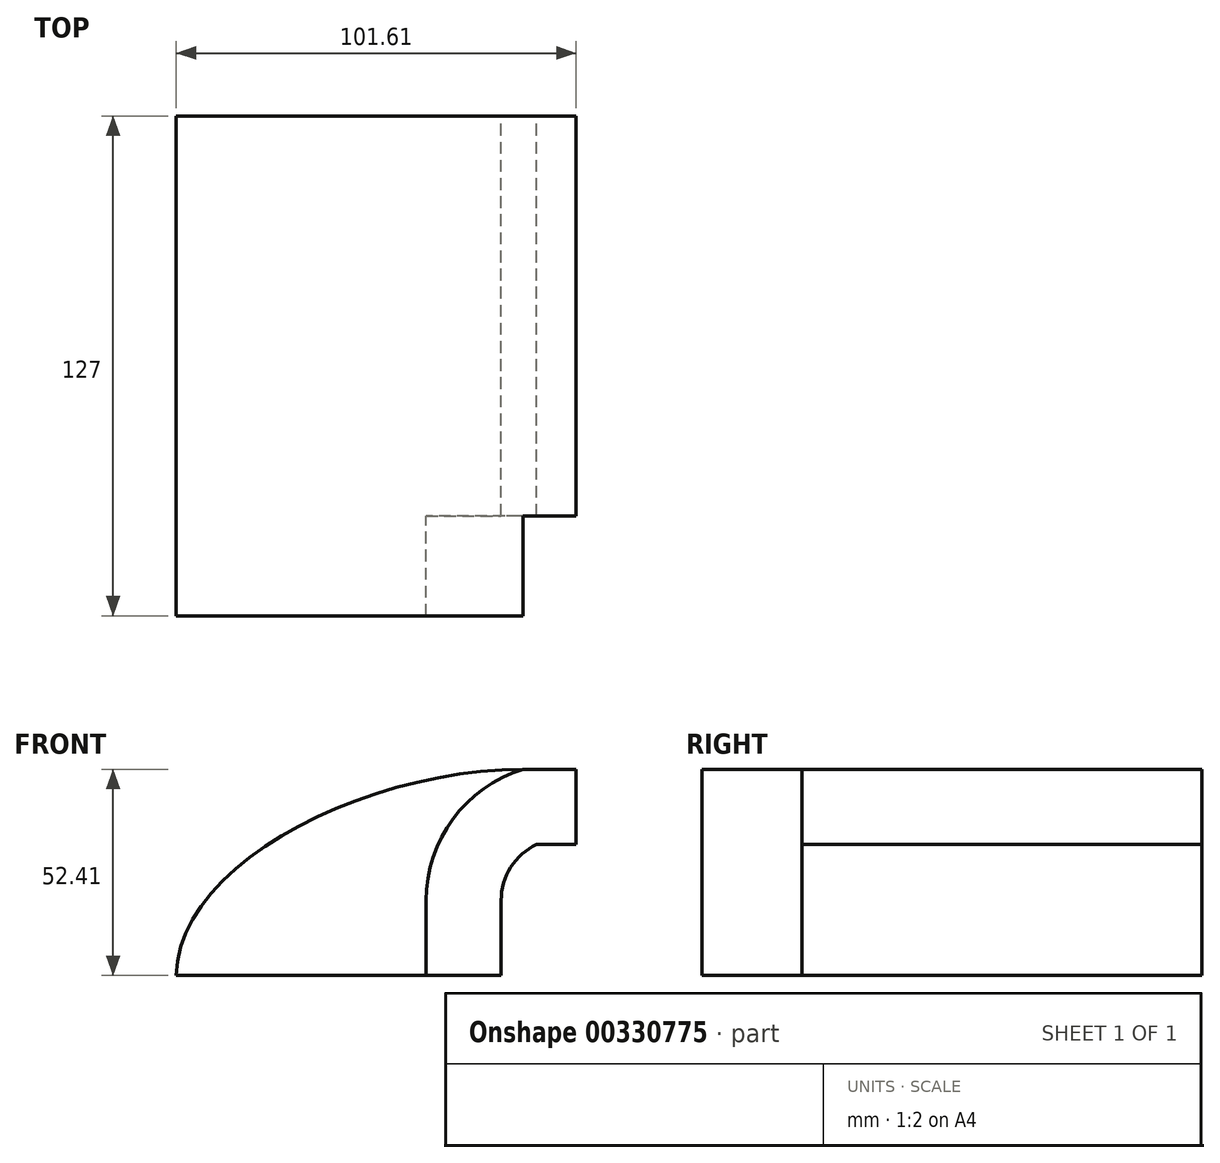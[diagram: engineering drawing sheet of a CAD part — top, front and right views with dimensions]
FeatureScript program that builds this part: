
annotation { "Feature Type Name" : "Feature", "Feature Type Description" : "" }
export const myFeature = defineFeature(function(context is Context, id is Id, definition is map)
    precondition{}
    {
        {
            var Q0;
            Q0=qCreatedBy(makeId("Front.planeOp"),FACE);
            var sketch = newSketch(context, id + "F0", { "sketchPlane" : qUnion([Q0])});
            skLineSegment(sketch, "E0.bottom", {"start": v(-41.28, 9.52) * mm, "end": v(41.28, 9.53) * mm});
            skLineSegment(sketch, "E0.top", {"start": v(-41.28, -9.53) * mm, "end": v(41.28, -9.53) * mm});
            skLineSegment(sketch, "E0.left", {"start": v(-41.28, 9.52) * mm, "end": v(-41.28, -9.53) * mm});
            skLineSegment(sketch, "E0.right", {"start": v(41.28, 9.53) * mm, "end": v(41.28, -9.52) * mm});
            skPoint(sketch, "E0.middle", {"position": v(0, 0) * mm});
            skLineSegment(sketch, "E1.bottom", {"start": v(111.13, 38.1) * mm, "end": v(60.32, 38.1) * mm});
            skLineSegment(sketch, "E1.top", {"start": v(111.12, 66.67) * mm, "end": v(60.32, 66.67) * mm});
            skLineSegment(sketch, "E1.left", {"start": v(111.12, 38.1) * mm, "end": v(111.12, 66.67) * mm});
            skLineSegment(sketch, "E1.right", {"start": v(60.32, 38.1) * mm, "end": v(60.32, 66.67) * mm});
            skPoint(sketch, "E1.middle", {"position": v(85.72, 52.39) * mm});
            skLineSegment(sketch, "E2", {"start": v(41.27, 9.53) * mm, "end": v(41.27, 28.56) * mm});
            skArc(sketch, "E3", {"start": v(50.29, 42.88) * mm, "mid": v(43.72, 37.02) * mm, "end": v(41.27, 28.56) * mm});
            skLineSegment(sketch, "E4", {"start": v(50.29, 42.88) * mm, "end": v(85.72, 42.88) * mm});
            skLineSegment(sketch, "E5.0", {"start": v(46.83, 61.93) * mm, "end": v(85.74, 61.93) * mm});
            skArc(sketch, "E5.1", {"start": v(46.83, 61.93) * mm, "mid": v(29.04, 49.29) * mm, "end": v(22.22, 28.56) * mm});
            skLineSegment(sketch, "E5.2", {"start": v(22.22, 9.53) * mm, "end": v(22.22, 28.56) * mm});
            skLineSegment(sketch, "E6", {"start": v(85.72, 66.67) * mm, "end": v(85.72, 42.88) * mm});
            skFitSpline(sketch, "E7", {"points": [v(-41.28, 9.52) * mm, v(46.83, 61.93) * mm], "startDerivative": vector(0.85, 84.5) * mm, "endDerivative": vector(122.22, 0.4) * mm});
            skSolve(sketch);
        }
        {
            var Q0;
            Q0=makeQuery(id+"F0.imprint","IMPRINT",FACE,{"disambiguationData":[TD([[makeQuery(id+"F0.imprint","IMPRINT",EDGE,{"derivedFrom":sQuery(id+"F0.wireOp",EDGE,"E5.1")}),-1.0]])]});
            extrude(context, id + "F1", {"entities" : qUnion([Q0]), "depth" : 25.4 * mm});
        }
        {
            var Q0;
            Q0=makeQuery(id+"F1.opExtrude","CAP_FACE",FACE,{"disambiguationData":[OSD([sQuery(id+"F0.wireOp",EDGE,"E0.bottom"),sQuery(id+"F0.wireOp",EDGE,"E5.1"),sQuery(id+"F0.wireOp",EDGE,"E5.2"),sQuery(id+"F0.wireOp",EDGE,"E7")])],"isStart":false});
            extrude(context, id + "F2", {"entities" : qUnion([Q0]), "operationType" : NewBodyOperationType.ADD, "depth" : 101.6 * mm});
        }
        {
            var Q0;
            {var subQ1=sQuery(id+"F0.wireOp",EDGE,"E2");Q0=makeQuery(id+"F0.imprint","IMPRINT",FACE,{"disambiguationData":[TD([[makeQuery(id+"F0.imprint","IMPRINT",EDGE,{"derivedFrom":subQ1}),1.0]])]});}
            extrude(context, id + "F3", {"entities" : qUnion([Q0]), "operationType" : NewBodyOperationType.ADD, "depth" : 101.6 * mm});
        }
    });
